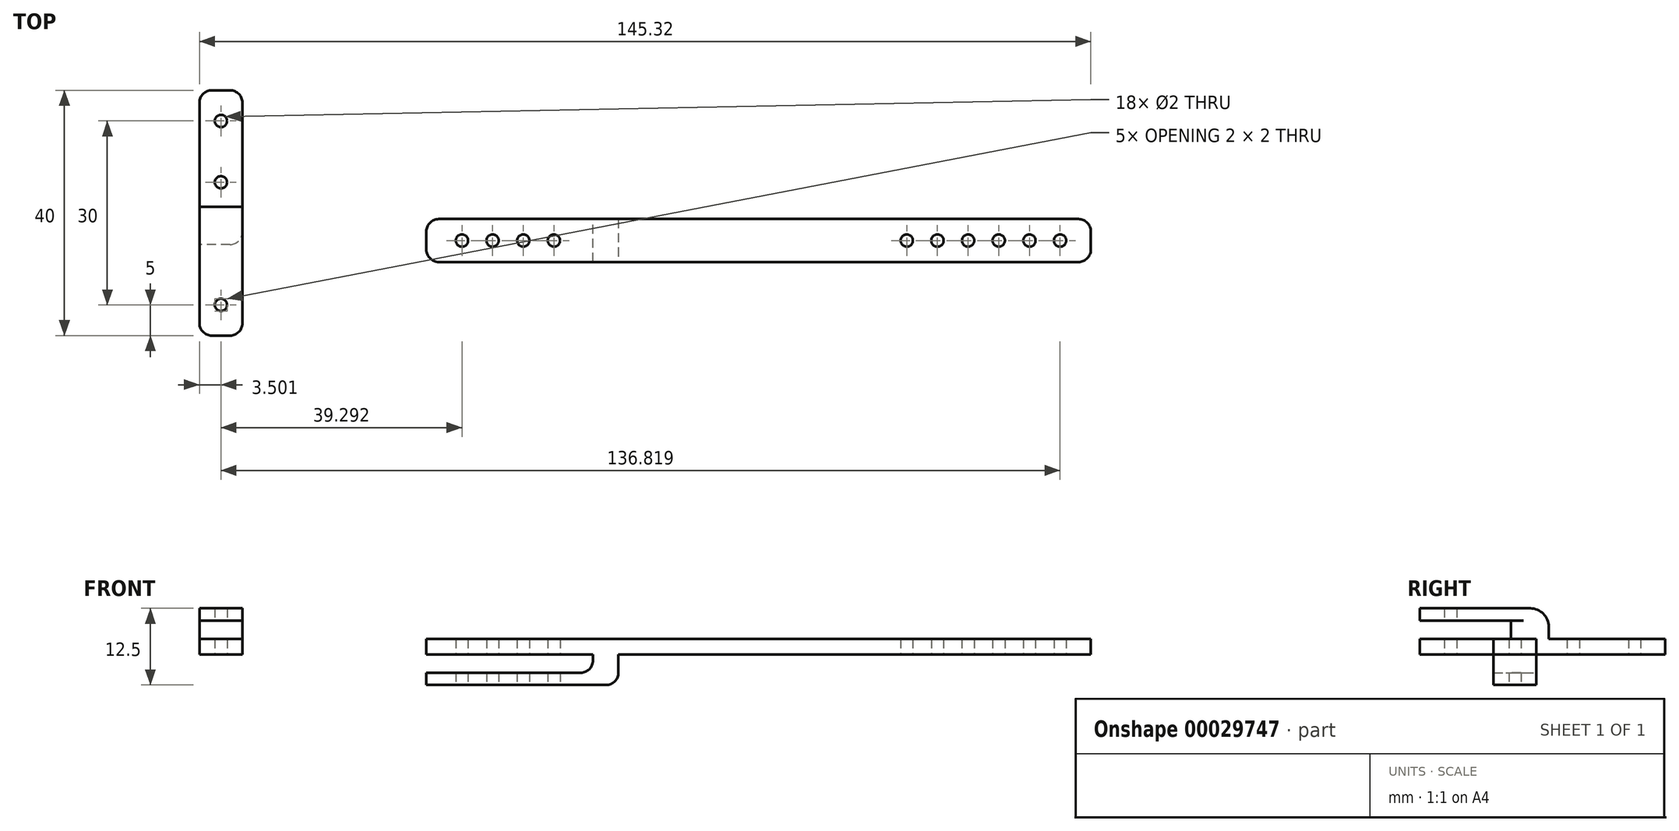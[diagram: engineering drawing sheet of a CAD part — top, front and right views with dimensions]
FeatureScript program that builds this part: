
annotation { "Feature Type Name" : "Feature", "Feature Type Description" : "" }
export const myFeature = defineFeature(function(context is Context, id is Id, definition is map)
    precondition{}
    {
        {
            var Q0;
            Q0=qCreatedBy(makeId("Top.planeOp"),FACE);
            var sketch = newSketch(context, id + "F0", { "sketchPlane" : qUnion([Q0])});
            skLineSegment(sketch, "E0.bottom", {"start": v(10.68, 0) * mm, "end": v(115, 0) * mm});
            skLineSegment(sketch, "E0.top", {"start": v(10.68, 7) * mm, "end": v(115, 7) * mm});
            skLineSegment(sketch, "E0.right", {"start": v(117, 2) * mm, "end": v(117, 5) * mm});
            skCircle(sketch, "E1", {"center": v(112, 3.5) * mm, "radius": 1 * mm});
            skPoint(sketch, "E1.centerSnap0", {"position": v(117, 3.5) * mm});
            skCircle(sketch, "E2", {"center": v(107, 3.5) * mm, "radius": 1 * mm});
            skCircle(sketch, "E3", {"center": v(102, 3.5) * mm, "radius": 1 * mm});
            skCircle(sketch, "E4", {"center": v(97, 3.5) * mm, "radius": 1 * mm});
            skCircle(sketch, "E5", {"center": v(92, 3.5) * mm, "radius": 1 * mm});
            skCircle(sketch, "E6", {"center": v(87, 3.5) * mm, "radius": 1 * mm});
            skCircle(sketch, "E7", {"center": v(29.47, 3.5) * mm, "radius": 1 * mm});
            skCircle(sketch, "E8", {"center": v(24.47, 3.5) * mm, "radius": 1 * mm});
            skCircle(sketch, "E9", {"center": v(19.47, 3.5) * mm, "radius": 1 * mm});
            skCircle(sketch, "E10", {"center": v(14.47, 3.5) * mm, "radius": 1 * mm});
            skLineSegment(sketch, "E11", {"start": v(8.68, 5) * mm, "end": v(8.68, 2) * mm});
            skPoint(sketch, "E12.orphan", {"position": v(0, 0) * mm});
            skPoint(sketch, "E13.visualSharp", {"position": v(8.68, 7) * mm});
            skArc(sketch, "E13.filletArc", {"start": v(10.68, 7) * mm, "mid": v(9.27, 6.41) * mm, "end": v(8.68, 5) * mm});
            skPoint(sketch, "E14.visualSharp", {"position": v(8.68, 0) * mm});
            skArc(sketch, "E14.filletArc", {"start": v(8.68, 2) * mm, "mid": v(9.27, 0.59) * mm, "end": v(10.68, 0) * mm});
            skPoint(sketch, "E15.visualSharp", {"position": v(117, 7) * mm});
            skArc(sketch, "E15.filletArc", {"start": v(117, 5) * mm, "mid": v(116.41, 6.41) * mm, "end": v(115, 7) * mm});
            skPoint(sketch, "E16.visualSharp", {"position": v(117, 0) * mm});
            skArc(sketch, "E16.filletArc", {"start": v(115, 0) * mm, "mid": v(116.41, 0.59) * mm, "end": v(117, 2) * mm});
            skSolve(sketch);
        }
        {
            var Q0;
            Q0=qCreatedBy(makeId("Top.planeOp"),FACE);
            var sketch = newSketch(context, id + "F1", { "sketchPlane" : qUnion([Q0])});
            skLineSegment(sketch, "E17.bottom", {"start": v(-28.32, 28) * mm, "end": v(-21.32, 28) * mm});
            skLineSegment(sketch, "E17.top", {"start": v(-28.32, -12) * mm, "end": v(-21.32, -12) * mm});
            skLineSegment(sketch, "E17.left", {"start": v(-28.32, 28) * mm, "end": v(-28.32, -12) * mm});
            skLineSegment(sketch, "E17.right", {"start": v(-21.32, 28) * mm, "end": v(-21.32, -12) * mm});
            skCircle(sketch, "E18", {"center": v(-24.82, -7) * mm, "radius": 1 * mm});
            skPoint(sketch, "E18.centerSnap0", {"position": v(-24.82, 28) * mm});
            skCircle(sketch, "E19", {"center": v(-24.82, 23) * mm, "radius": 1 * mm});
            skCircle(sketch, "E20", {"center": v(-24.82, 13) * mm, "radius": 1 * mm});
            skSolve(sketch);
        }
        {
            var Q0;
            Q0 = qSketchRegion(id + "F1", true);
            extrude(context, id + "F2", {"entities" : qUnion([Q0]), "depth" : 2.5 * mm});
        }
        {
            var Q0;
            Q0=makeQuery(id+"F0.imprint","IMPRINT",FACE,{"disambiguationData":[TD([[makeQuery(id+"F0.imprint","IMPRINT",EDGE,{"derivedFrom":sQuery(id+"F0.wireOp",EDGE,"E0.bottom")}),1.0]])]});
            extrude(context, id + "F3", {"entities" : qUnion([Q0]), "depth" : 2.5 * mm});
        }
        {
            var Q0;
            Q0=makeQuery(id+"F2.opExtrude","SWEPT_EDGE",EDGE,{"disambiguationData":[OSD([sQuery(id+"F1.wireOp",EDGE,"E17.bottom"),sQuery(id+"F1.wireOp",EDGE,"E17.right")])]});
            var Q1;
            Q1=makeQuery(id+"F2.opExtrude","SWEPT_EDGE",EDGE,{"disambiguationData":[OSD([sQuery(id+"F1.wireOp",EDGE,"E17.top"),sQuery(id+"F1.wireOp",EDGE,"E17.right")])]});
            var Q2;
            Q2=makeQuery(id+"F2.opExtrude","SWEPT_EDGE",EDGE,{"disambiguationData":[OSD([sQuery(id+"F1.wireOp",EDGE,"E17.top"),sQuery(id+"F1.wireOp",EDGE,"E17.left")])]});
            var Q3;
            Q3=makeQuery(id+"F2.opExtrude","SWEPT_EDGE",EDGE,{"disambiguationData":[OSD([sQuery(id+"F1.wireOp",EDGE,"E17.bottom"),sQuery(id+"F1.wireOp",EDGE,"E17.left")])]});
            fillet(context, id + "F4", {"entities" : qUnion([Q0, Q1, Q2, Q3]), "radius" : 2 * mm, "tangentPropagation" : true, "allowEdgeOverflow" : false});
        }
        {
            var Q0;
            Q0=makeQuery(id+"F2.opExtrude","CAP_FACE",FACE,{"disambiguationData":[OSD([sQuery(id+"F1.wireOp",EDGE,"E17.bottom"),sQuery(id+"F1.wireOp",EDGE,"E17.top"),sQuery(id+"F1.wireOp",EDGE,"E17.left"),sQuery(id+"F1.wireOp",EDGE,"E17.right"),sQuery(id+"F1.wireOp",EDGE,"E18"),sQuery(id+"F1.wireOp",EDGE,"E19"),sQuery(id+"F1.wireOp",EDGE,"E20")])],"isStart":false});
            var sketch = newSketch(context, id + "F5", { "sketchPlane" : qUnion([Q0])});
            skLineSegment(sketch, "E21.0", {"start": v(-21.32, 26) * mm, "end": v(-21.32, -10) * mm});
            skLineSegment(sketch, "E22.0", {"start": v(-28.32, 26) * mm, "end": v(-28.32, -10) * mm});
            skArc(sketch, "E23.0", {"start": v(-28.32, -10) * mm, "mid": v(-27.73, -11.41) * mm, "end": v(-26.32, -12) * mm});
            skLineSegment(sketch, "E24.0", {"start": v(-26.32, -12) * mm, "end": v(-23.32, -12) * mm});
            skArc(sketch, "E25.0", {"start": v(-23.32, -12) * mm, "mid": v(-21.9, -11.41) * mm, "end": v(-21.32, -10) * mm});
            skLineSegment(sketch, "E26", {"start": v(-21.32, 6) * mm, "end": v(-28.32, 6) * mm});
            skLineSegment(sketch, "E27", {"start": v(-21.32, 6) * mm, "end": v(-21.32, -10) * mm});
            skLineSegment(sketch, "E28", {"start": v(-28.32, 6) * mm, "end": v(-28.32, -10) * mm});
            skSolve(sketch);
        }
        {
            var Q0;
            Q0=makeQuery(id+"F5.imprint","IMPRINT",FACE,{"disambiguationData":[TD([[makeQuery(id+"F5.imprint","IMPRINT",EDGE,{"derivedFrom":sQuery(id+"F5.wireOp",EDGE,"E23.0")}),1.0]])]});
            extrude(context, id + "F6", {"entities" : qUnion([Q0]), "operationType" : NewBodyOperationType.ADD, "depth" : 5 * mm});
        }
        {
            var Q0;
            Q0=makeQuery(id+"F6.boolean.opBoolean","MERGE",FACE,{"derivedFrom":[makeQuery(id+"F2.opExtrude","SWEPT_FACE",FACE,{"disambiguationData":[OSD([sQuery(id+"F1.wireOp",EDGE,"E17.left")])]}),makeQuery(id+"F6.opExtrude","SWEPT_FACE",FACE,{"disambiguationData":[OSD([sQuery(id+"F5.wireOp",EDGE,"E28")])]})]});
            var sketch = newSketch(context, id + "F7", { "sketchPlane" : qUnion([Q0])});
            skLineSegment(sketch, "E29.bottom", {"start": v(-2.85, 5.5) * mm, "end": v(13.15, 5.5) * mm});
            skLineSegment(sketch, "E29.top", {"start": v(-2.85, 2.5) * mm, "end": v(13.15, 2.5) * mm});
            skLineSegment(sketch, "E29.left", {"start": v(-2.85, 5.5) * mm, "end": v(-2.85, 2.5) * mm});
            skLineSegment(sketch, "E29.right", {"start": v(13.15, 5.5) * mm, "end": v(13.15, 2.5) * mm});
            skSolve(sketch);
        }
        {
            var Q0;
            Q0 = qSketchRegion(id + "F7", true);
            extrude(context, id + "F8", {"entities" : qUnion([Q0]), "operationType" : NewBodyOperationType.REMOVE, "oppositeDirection" : true, "depth" : 25 * mm});
        }
        {
            var Q0;
            Q0=makeQuery(id+"F8.boolean.opBoolean","COPY",EDGE,{"derivedFrom":makeQuery(id+"F8.opExtrude","CAP_EDGE",EDGE,{"disambiguationData":[OSD([sQuery(id+"F7.wireOp",EDGE,"E29.left")])],"isStart":true})});
            var Q1;
            Q1=makeQuery(id+"F8.boolean.opBoolean","INTERSECT",EDGE,{"derivedFrom":[makeQuery(id+"F6.boolean.opBoolean","MERGE",FACE,{"derivedFrom":[makeQuery(id+"F2.opExtrude","SWEPT_FACE",FACE,{"disambiguationData":[OSD([sQuery(id+"F1.wireOp",EDGE,"E17.right")])]}),makeQuery(id+"F6.opExtrude","SWEPT_FACE",FACE,{"disambiguationData":[OSD([sQuery(id+"F5.wireOp",EDGE,"E27")])]})]}),makeQuery(id+"F8.opExtrude","SWEPT_FACE",FACE,{"disambiguationData":[OSD([sQuery(id+"F7.wireOp",EDGE,"E29.left")])]})]});
            fillet(context, id + "F9", {"entities" : qUnion([Q0, Q1]), "radius" : 2 * mm, "tangentPropagation" : true, "allowEdgeOverflow" : false});
        }
        {
            var Q0;
            Q0=makeQuery(id+"F6.opExtrude","SWEPT_FACE",FACE,{"disambiguationData":[OSD([sQuery(id+"F5.wireOp",EDGE,"E26")])]});
            extrude(context, id + "F10", {"entities" : qUnion([Q0]), "operationType" : NewBodyOperationType.ADD, "depth" : 3 * mm});
        }
        {
            var Q0;
            {var subQ0=sQuery(id+"F5.wireOp",EDGE,"E26");Q0=makeQuery(id+"F10.opExtrude","CAP_EDGE",EDGE,{"disambiguationData":[OSD([subQ0]),TDD([makeQuery(id+"F6.opExtrude","CAP_EDGE",EDGE,{"disambiguationData":[OSD([subQ0])],"isStart":false})])],"isStart":false});}
            fillet(context, id + "F11", {"entities" : qUnion([Q0]), "radius" : 3 * mm, "tangentPropagation" : true, "allowEdgeOverflow" : false});
        }
        {
            var Q0;
            Q0=makeQuery(id+"F0.imprint","IMPRINT",FACE,{"disambiguationData":[TD([[makeQuery(id+"F0.imprint","IMPRINT",EDGE,{"derivedFrom":sQuery(id+"F0.wireOp",EDGE,"E0.bottom")}),1.0]])]});
            var sketch = newSketch(context, id + "F12", { "sketchPlane" : qUnion([Q0])});
            skArc(sketch, "E30.0.0", {"start": v(8.68, 2) * mm, "mid": v(9.27, 0.59) * mm, "end": v(10.68, 0) * mm});
            skLineSegment(sketch, "E30.0.1", {"start": v(10.68, 0) * mm, "end": v(39.99, 0) * mm});
            skArc(sketch, "E30.0.2", {"start": v(115, 0) * mm, "mid": v(116.41, 0.59) * mm, "end": v(117, 2) * mm});
            skLineSegment(sketch, "E30.0.3", {"start": v(117, 2) * mm, "end": v(117, 5) * mm});
            skArc(sketch, "E30.0.4", {"start": v(117, 5) * mm, "mid": v(116.41, 6.41) * mm, "end": v(115, 7) * mm});
            skLineSegment(sketch, "E30.0.5", {"start": v(39.99, 7) * mm, "end": v(10.68, 7) * mm});
            skArc(sketch, "E30.0.6", {"start": v(10.68, 7) * mm, "mid": v(9.27, 6.41) * mm, "end": v(8.68, 5) * mm});
            skLineSegment(sketch, "E30.0.7", {"start": v(8.68, 5) * mm, "end": v(8.68, 2) * mm});
            skLineSegment(sketch, "E31", {"start": v(39.99, 7) * mm, "end": v(39.99, 0) * mm});
            skSolve(sketch);
        }
        {
            var Q0;
            Q0=makeQuery(id+"F12.imprint","IMPRINT",FACE,{"disambiguationData":[TD([[makeQuery(id+"F12.imprint","IMPRINT",EDGE,{"derivedFrom":sQuery(id+"F12.wireOp",EDGE,"E30.0.0")}),1.0]])]});
            extrude(context, id + "F13", {"entities" : qUnion([Q0]), "operationType" : NewBodyOperationType.ADD, "oppositeDirection" : true, "depth" : 5 * mm});
        }
        {
            var Q0;
            Q0=makeQuery(id+"F13.boolean.opBoolean","MERGE",FACE,{"derivedFrom":[makeQuery(id+"F3.opExtrude","SWEPT_FACE",FACE,{"disambiguationData":[OSD([sQuery(id+"F0.wireOp",EDGE,"E0.top")])]}),makeQuery(id+"F13.opExtrude","SWEPT_FACE",FACE,{"disambiguationData":[OSD([sQuery(id+"F12.wireOp",EDGE,"E30.0.5")])]})]});
            var sketch = newSketch(context, id + "F14", { "sketchPlane" : qUnion([Q0])});
            skLineSegment(sketch, "E32.bottom", {"start": v(-35.83, 0) * mm, "end": v(-6.7, 0) * mm});
            skLineSegment(sketch, "E32.top", {"start": v(-35.83, -3) * mm, "end": v(-6.7, -3) * mm});
            skLineSegment(sketch, "E32.left", {"start": v(-35.83, 0) * mm, "end": v(-35.83, -3) * mm});
            skLineSegment(sketch, "E32.right", {"start": v(-6.7, 0) * mm, "end": v(-6.7, -3) * mm});
            skLineSegment(sketch, "E33.0", {"start": v(-10.68, 2.5) * mm, "end": v(-115, 2.5) * mm});
            skSolve(sketch);
        }
        {
            var Q0;
            Q0 = qSketchRegion(id + "F14", true);
            extrude(context, id + "F15", {"entities" : qUnion([Q0]), "operationType" : NewBodyOperationType.REMOVE, "oppositeDirection" : true, "depth" : 25 * mm});
        }
        {
            var Q0;
            Q0=makeQuery(id+"F13.opExtrude","CAP_EDGE",EDGE,{"disambiguationData":[OSD([sQuery(id+"F12.wireOp",EDGE,"E31")])],"isStart":true});
            var Q1;
            Q1=makeQuery(id+"F15.boolean.opBoolean","COPY",EDGE,{"derivedFrom":makeQuery(id+"F15.opExtrude","SWEPT_EDGE",EDGE,{"disambiguationData":[OSD([sQuery(id+"F14.wireOp",EDGE,"E32.top"),sQuery(id+"F14.wireOp",EDGE,"E32.left")])]})});
            var Q2;
            Q2=makeQuery(id+"F13.opExtrude","CAP_EDGE",EDGE,{"disambiguationData":[OSD([sQuery(id+"F12.wireOp",EDGE,"E31")])],"isStart":false});
            fillet(context, id + "F16", {"entities" : qUnion([Q0, Q1, Q2]), "radius" : 2 * mm, "tangentPropagation" : true, "allowEdgeOverflow" : false});
        }
    });
